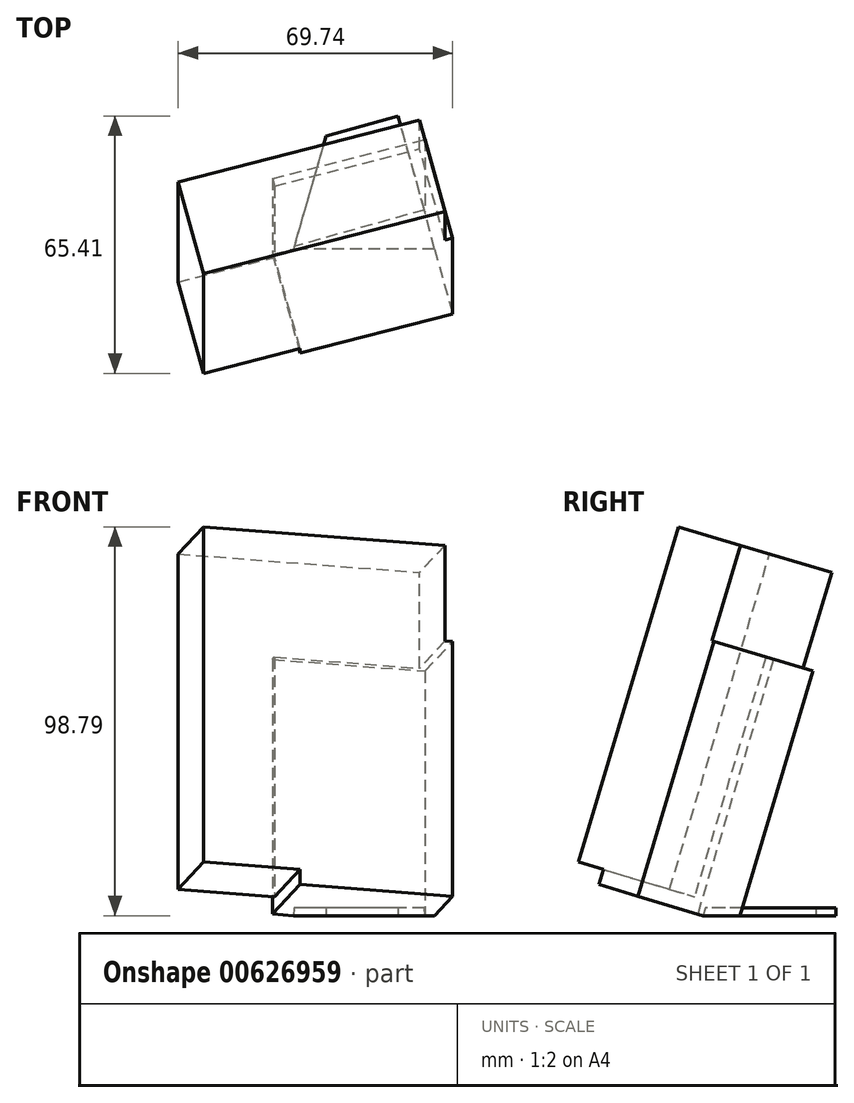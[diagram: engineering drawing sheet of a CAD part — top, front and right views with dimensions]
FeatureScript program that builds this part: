
annotation { "Feature Type Name" : "Feature", "Feature Type Description" : "" }
export const myFeature = defineFeature(function(context is Context, id is Id, definition is map)
    precondition{}
    {
        {
            var Q0;
            Q0=qCreatedBy(makeId("Right.planeOp"),FACE);
            var sketch = newSketch(context, id + "F0", { "sketchPlane" : qUnion([Q0])});
            skLineSegment(sketch, "E0", {"start": v(0, 0) * mm, "end": v(25.4, 85.2) * mm});
            skLineSegment(sketch, "E1", {"start": v(0, 0) * mm, "end": v(25.4, 0) * mm});
            skLineSegment(sketch, "E2", {"start": v(25.4, 85.2) * mm, "end": v(25.4, 0) * mm});
            skSolve(sketch);
        }
        {
            var Q0;
            Q0=qCreatedBy(makeId("Front.planeOp"),FACE);
            var Q1;
            Q1=sQuery(id+"F0.wireOp",EDGE,"E0");
            cPlane(context, id + "F1", {"entities" : qUnion([Q0, Q1]), "cplaneType" : CPlaneType.LINE_ANGLE, "offset" : 25 * mm, "angle" : 15 * degree, "width" : 150 * mm, "height" : 150 * mm});
        }
        {
            var Q0;
            Q0=qCreatedBy(id+"F1.planeOp",FACE);
            var sketch = newSketch(context, id + "F2", { "sketchPlane" : qUnion([Q0])});
            skLineSegment(sketch, "E3.bottom", {"start": v(0, 0) * mm, "end": v(-63.5, 0) * mm});
            skLineSegment(sketch, "E3.top", {"start": v(0, 88.9) * mm, "end": v(-63.5, 88.9) * mm});
            skLineSegment(sketch, "E3.left", {"start": v(0, 0) * mm, "end": v(0, 88.9) * mm});
            skLineSegment(sketch, "E3.right", {"start": v(-63.5, 0) * mm, "end": v(-63.5, 88.9) * mm});
            skSolve(sketch);
        }
        {
            var Q0;
            Q0=makeQuery(id+"F2.imprint","IMPRINT",FACE,{"disambiguationData":[TD([[makeQuery(id+"F2.imprint","IMPRINT",EDGE,{"derivedFrom":sQuery(id+"F2.wireOp",EDGE,"E3.bottom")}),-1.0]])]});
            extrude(context, id + "F3", {"entities" : qUnion([Q0]), "oppositeDirection" : true, "depth" : 25 * mm, "offsetDistance" : 25 * mm});
        }
        {
            var Q0;
            Q0=qCreatedBy(makeId("Top.planeOp"),FACE);
            var Q1;
            Q1=makeQuery(id+"F3.opExtrude","CAP_VERTEX",VERTEX,{"disambiguationData":[OSD([sQuery(id+"F2.wireOp",EDGE,"E3.bottom"),sQuery(id+"F2.wireOp",EDGE,"E3.right")])],"isStart":true});
            cPlane(context, id + "F4", {"entities" : qUnion([Q0, Q1]), "cplaneType" : CPlaneType.PLANE_POINT, "offset" : 25 * mm, "width" : 150 * mm, "height" : 150 * mm});
        }
        {
            var Q0;
            Q0=qCreatedBy(id+"F1.planeOp",FACE);
            var sketch = newSketch(context, id + "F5", { "sketchPlane" : qUnion([Q0])});
            skLineSegment(sketch, "E4.bottom", {"start": v(-25.4, 63.5) * mm, "end": v(-65.5, 63.5) * mm});
            skLineSegment(sketch, "E4.top", {"start": v(-25.4, -4) * mm, "end": v(-65.5, -4) * mm});
            skLineSegment(sketch, "E4.left", {"start": v(-25.4, 63.5) * mm, "end": v(-25.4, -4) * mm});
            skLineSegment(sketch, "E4.right", {"start": v(-65.5, 63.5) * mm, "end": v(-65.5, -4) * mm});
            skLineSegment(sketch, "E5.0", {"start": v(-63.5, 0) * mm, "end": v(-63.5, 88.9) * mm});
            skLineSegment(sketch, "E5.1", {"start": v(0, 0) * mm, "end": v(-63.5, 0) * mm});
            skSolve(sketch);
        }
        {
            var Q0;
            Q0=makeQuery(id+"F5.imprint","IMPRINT",FACE,{"disambiguationData":[TD([[makeQuery(id+"F5.imprint","IMPRINT",EDGE,{"derivedFrom":sQuery(id+"F5.wireOp",EDGE,"E4.bottom")}),1.0]])]});
            var Q1;
            {var subQ2=sQuery(id+"F5.wireOp",EDGE,"E4.top");Q1=makeQuery(id+"F5.imprint","IMPRINT",FACE,{"disambiguationData":[TD([[makeQuery(id+"F5.imprint","IMPRINT",EDGE,{"derivedFrom":subQ2}),-1.0]])]});}
            extrude(context, id + "F6", {"entities" : qUnion([Q0, Q1]), "depth" : 2.1 * mm, "offsetDistance" : 25 * mm});
        }
        {
            var Q0;
            {var subQ2=sQuery(id+"F5.wireOp",EDGE,"E4.top");Q0=makeQuery(id+"F5.imprint","IMPRINT",FACE,{"disambiguationData":[TD([[makeQuery(id+"F5.imprint","IMPRINT",EDGE,{"derivedFrom":subQ2}),-1.0]])]});}
            extrude(context, id + "F7", {"entities" : qUnion([Q0]), "operationType" : NewBodyOperationType.ADD, "oppositeDirection" : true, "depth" : 25 * mm, "offsetDistance" : 25 * mm});
        }
        {
            var Q0;
            Q0=qCreatedBy(id+"F4.planeOp",FACE);
            cPlane(context, id + "F8", {"entities" : qUnion([Q0]), "cplaneType" : CPlaneType.OFFSET, "offset" : 2 * mm, "oppositeDirection" : true, "width" : 150 * mm, "height" : 150 * mm});
        }
        {
            var Q0;
            Q0=qCreatedBy(id+"F8.planeOp",FACE);
            var sketch = newSketch(context, id + "F9", { "sketchPlane" : qUnion([Q0])});
            skLineSegment(sketch, "E6.0", {"start": v(31, -17.98) * mm, "end": v(69.74, -8.04) * mm});
            skLineSegment(sketch, "E6.1", {"start": v(24, 7.1) * mm, "end": v(31, -17.98) * mm});
            skLineSegment(sketch, "E6.2", {"start": v(24, 7.1) * mm, "end": v(62.72, 17.05) * mm});
            skLineSegment(sketch, "E6.3", {"start": v(62.72, 17.05) * mm, "end": v(69.74, -8.04) * mm});
            skLineSegment(sketch, "E7.0", {"start": v(24, 26.39) * mm, "end": v(62.72, 36.33) * mm});
            skLineSegment(sketch, "E8", {"start": v(69.74, -8.04) * mm, "end": v(62.72, 36.33) * mm});
            skLineSegment(sketch, "E9", {"start": v(24, 7.1) * mm, "end": v(24, 26.39) * mm});
            skSolve(sketch);
        }
        {
            var Q0;
            Q0=makeQuery(id+"F9.imprint","IMPRINT",FACE,{"disambiguationData":[TD([[makeQuery(id+"F9.imprint","IMPRINT",EDGE,{"derivedFrom":sQuery(id+"F9.wireOp",EDGE,"E6.2")}),1.0]])]});
            var Q1;
            Q1=makeQuery(id+"F9.imprint","IMPRINT",FACE,{"disambiguationData":[TD([[makeQuery(id+"F9.imprint","IMPRINT",EDGE,{"derivedFrom":sQuery(id+"F9.wireOp",EDGE,"E6.0")}),1.0]])]});
            extrude(context, id + "F10", {"entities" : qUnion([Q0, Q1]), "operationType" : NewBodyOperationType.REMOVE, "oppositeDirection" : true, "depth" : 25 * mm, "offsetDistance" : 25 * mm});
        }
        {
            var Q0;
            Q0=makeQuery(id+"F10.boolean.opBoolean","COPY",FACE,{"derivedFrom":makeQuery(id+"F10.opExtrude","CAP_FACE",FACE,{"disambiguationData":[OSD([sQuery(id+"F9.wireOp",EDGE,"E6.0"),sQuery(id+"F9.wireOp",EDGE,"E6.1"),sQuery(id+"F9.wireOp",EDGE,"E7.0"),sQuery(id+"F9.wireOp",EDGE,"E8"),sQuery(id+"F9.wireOp",EDGE,"E9")])],"isStart":true})});
            var sketch = newSketch(context, id + "F11", { "sketchPlane" : qUnion([Q0])});
            skLineSegment(sketch, "E10", {"start": v(62.72, -17.81) * mm, "end": v(55.88, -42.27) * mm});
            skLineSegment(sketch, "E11", {"start": v(55.88, -42.27) * mm, "end": v(37.54, -37.14) * mm});
            skLineSegment(sketch, "E12", {"start": v(37.54, -37.14) * mm, "end": v(29.28, -8.46) * mm});
            skLineSegment(sketch, "E13", {"start": v(29.28, -8.46) * mm, "end": v(62.72, -17.81) * mm});
            skSolve(sketch);
        }
        {
            var Q0;
            Q0=makeQuery(id+"F11.imprint","IMPRINT",FACE,{"disambiguationData":[TD([[makeQuery(id+"F11.imprint","IMPRINT",EDGE,{"derivedFrom":sQuery(id+"F11.wireOp",EDGE,"E10")}),-1.0]])]});
            extrude(context, id + "F12", {"entities" : qUnion([Q0]), "operationType" : NewBodyOperationType.ADD, "oppositeDirection" : true, "depth" : 2 * mm, "offsetDistance" : 25 * mm});
        }
    });
